# Revit family: QF_Kelvinator_738254_KCHPT92.12_3-Door_Pizza_Prep_Table_94_Long
name_source: partatom
category: Specialty Equipment
units: mm (PartAtom-declared; Revit-internal decimal feet)

## family parameters
Always vertical = Yes
Cut with Voids When Loaded = No
Part Type = Normal
Room Calculation Point = No
Round Connector Dimension = Use Diameter
Shared = No
Work Plane-Based = No

## types (1)
- QF_Kelvinator_738254_KCHPT92.12_3-Door_Pizza_Prep_Table_94_Long
    Apparent Power = 0 VA
    Conn Conduit = Yes
    Conn Plug = 5-15P
    Cycle = 60 Hz
    Default Elevation = 0"
    Depth = 32 1/4"
    Description = 3-Door Pizza Prep Table 94" Long
    Elec Conn Connection Height = 0"
    Elec Conn RI Height = 0"
    FL Amps = 6 A
    Foodservice Equipment Identifier = Yes
    HP = 3/4
    Height = 41 5/16"
    Identify Quantity as Lot = Yes
    Item Number = 738254
    Length = 94 3/16"
    Manufacturer = Kelvinator Commercial
    Max Overcurrent Protection = 0 A
    Min Ckt Ampacity = 0 A
    Model = 738254 (KCHPT92.12)
    Number of Poles = 1
    Phase = 1
    Refrigerant Type = R290
    Volts = 115 V
    Watts = 900 W
    Weight in Pounds = 350.535

## geometry (parser evidence)
native form markers: Sweep x10
no freeform markers — native parametric forms only
